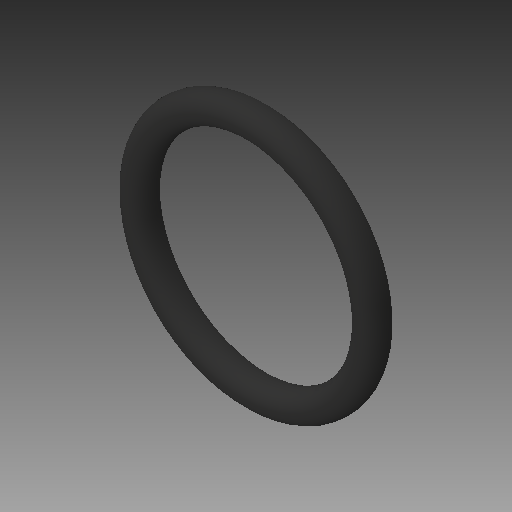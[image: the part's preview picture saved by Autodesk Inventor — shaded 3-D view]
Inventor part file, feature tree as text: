
AUTODESK INVENTOR PART (.ipt)
format: ipt  version: 2018 (Build 220112000, 112)  size: 135,168 bytes
history: native  units: in
note: dims shown in document units (in); Inventor stores cm internally (conversion verified against a paired STEP export)
features: revolve x1
ambient origin geometry x8: Origin, YZ Plane, XZ Plane, XY Plane, X Axis, Y Axis, Z Axis, Center Point
bodies: Solid1 (feature_tree)
feature tree (1):
  revolve  "Revolve1"  [1 undecoded]
note: 1 required parameter value undecoded (feature->parameter linkage not recoverable at this tier; creation-order binding heuristic only, values carry confidence <= 0.55)
